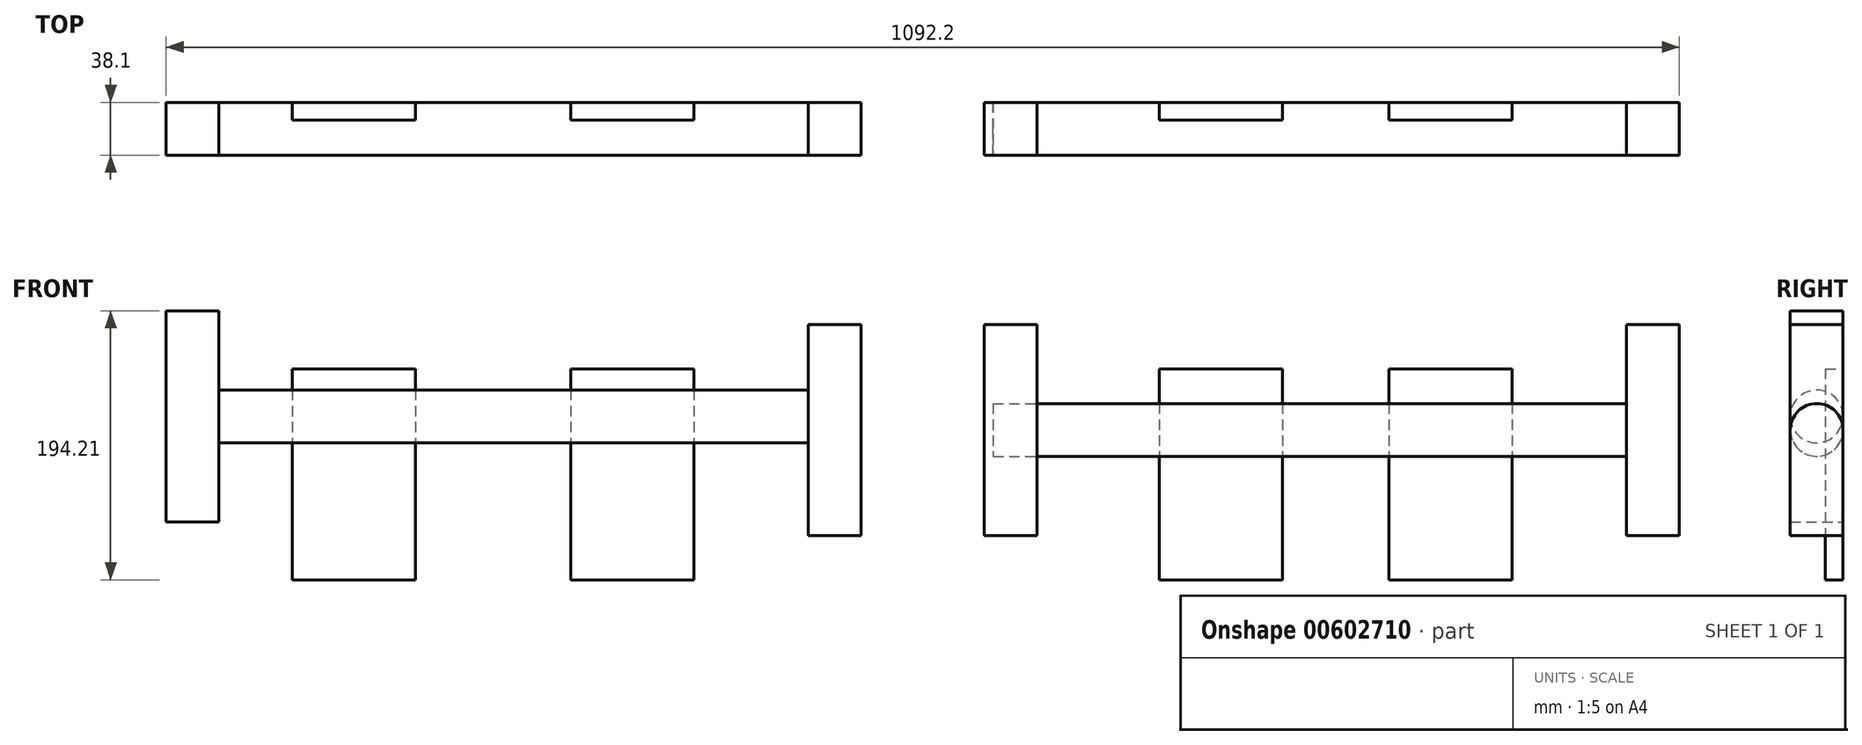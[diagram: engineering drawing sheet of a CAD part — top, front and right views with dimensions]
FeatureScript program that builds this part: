
annotation { "Feature Type Name" : "Feature", "Feature Type Description" : "" }
export const myFeature = defineFeature(function(context is Context, id is Id, definition is map)
    precondition{}
    {
        {
            var Q0;
            Q0=qCreatedBy(makeId("Front.planeOp"),FACE);
            var sketch = newSketch(context, id + "F0", { "sketchPlane" : qUnion([Q0])});
            skLineSegment(sketch, "E0.bottom", {"start": v(-201.81, 41.8) * mm, "end": v(-163.71, 41.8) * mm});
            skLineSegment(sketch, "E0.top", {"start": v(-201.81, -110.6) * mm, "end": v(-163.71, -110.6) * mm});
            skLineSegment(sketch, "E0.left", {"start": v(-201.81, 41.8) * mm, "end": v(-201.81, -110.6) * mm});
            skLineSegment(sketch, "E0.right", {"start": v(-163.71, 41.8) * mm, "end": v(-163.71, -110.6) * mm});
            skLineSegment(sketch, "E1.bottom", {"start": v(261.74, 32.02) * mm, "end": v(299.84, 32.02) * mm});
            skLineSegment(sketch, "E1.top", {"start": v(261.74, -120.38) * mm, "end": v(299.84, -120.38) * mm});
            skLineSegment(sketch, "E1.left", {"start": v(261.74, 32.02) * mm, "end": v(261.74, -120.38) * mm});
            skLineSegment(sketch, "E1.right", {"start": v(299.84, 32.02) * mm, "end": v(299.84, -120.38) * mm});
            skLineSegment(sketch, "E2.bottom", {"start": v(388.74, 32.02) * mm, "end": v(426.84, 32.02) * mm});
            skLineSegment(sketch, "E2.top", {"start": v(388.74, -120.38) * mm, "end": v(426.84, -120.38) * mm});
            skLineSegment(sketch, "E2.left", {"start": v(388.74, 32.02) * mm, "end": v(388.74, -120.38) * mm});
            skLineSegment(sketch, "E2.right", {"start": v(426.84, 32.02) * mm, "end": v(426.84, -120.38) * mm});
            skLineSegment(sketch, "E3.bottom", {"start": v(852.29, 32.02) * mm, "end": v(890.39, 32.02) * mm});
            skLineSegment(sketch, "E3.top", {"start": v(852.29, -120.38) * mm, "end": v(890.39, -120.38) * mm});
            skLineSegment(sketch, "E3.left", {"start": v(852.29, 32.02) * mm, "end": v(852.29, -120.38) * mm});
            skLineSegment(sketch, "E3.right", {"start": v(890.39, 32.02) * mm, "end": v(890.39, -120.38) * mm});
            skLineSegment(sketch, "E4", {"start": v(261.74, 32.02) * mm, "end": v(919.35, 32.02) * mm, "construction": true});
            skPoint(sketch, "E4.endSnap0", {"position": v(407.79, 32.02) * mm});
            skLineSegment(sketch, "E5", {"start": v(-201.81, 41.8) * mm, "end": v(299.84, 32.02) * mm, "construction": true});
            skSolve(sketch);
        }
        {
            var Q0;
            Q0=makeQuery(id+"F0.imprint","IMPRINT",FACE,{"disambiguationData":[TD([[makeQuery(id+"F0.imprint","IMPRINT",EDGE,{"derivedFrom":sQuery(id+"F0.wireOp",EDGE,"E0.bottom")}),-1.0]])]});
            var Q1;
            Q1=makeQuery(id+"F0.imprint","IMPRINT",FACE,{"disambiguationData":[TD([[makeQuery(id+"F0.imprint","IMPRINT",EDGE,{"derivedFrom":sQuery(id+"F0.wireOp",EDGE,"E1.bottom")}),-1.0]])]});
            var Q2;
            Q2=makeQuery(id+"F0.imprint","IMPRINT",FACE,{"disambiguationData":[TD([[makeQuery(id+"F0.imprint","IMPRINT",EDGE,{"derivedFrom":sQuery(id+"F0.wireOp",EDGE,"E2.bottom")}),-1.0]])]});
            var Q3;
            Q3=makeQuery(id+"F0.imprint","IMPRINT",FACE,{"disambiguationData":[TD([[makeQuery(id+"F0.imprint","IMPRINT",EDGE,{"derivedFrom":sQuery(id+"F0.wireOp",EDGE,"E3.bottom")}),-1.0]])]});
            extrude(context, id + "F1", {"entities" : qUnion([Q0, Q1, Q2, Q3]), "depth" : 38.1 * mm, "offsetDistance" : 25.4 * mm});
        }
        {
            var Q0;
            Q0=makeQuery(id+"F1.opExtrude","SWEPT_FACE",FACE,{"disambiguationData":[OSD([sQuery(id+"F0.wireOp",EDGE,"E0.right")])]});
            var sketch = newSketch(context, id + "F2", { "sketchPlane" : qUnion([Q0])});
            skCircle(sketch, "E6", {"center": v(-19.05, -34.4) * mm, "radius": 19.05 * mm});
            skPoint(sketch, "E6.centerSnap0", {"position": v(0, -34.4) * mm});
            skPoint(sketch, "E6.centerSnap1", {"position": v(-19.05, -110.6) * mm});
            skSolve(sketch);
        }
        {
            var Q0;
            {var subQ0=sQuery(id+"F2.wireOp",EDGE,"E6");var subQ1=sQuery(id+"F0.wireOp",EDGE,"E0.right");var subQ2=makeQuery(id+"F2.imprint","INTERSECT",VERTEX,{"derivedFrom":[makeQuery(id+"F1.opExtrude","CAP_EDGE",EDGE,{"disambiguationData":[OSD([subQ1])],"isStart":true}),subQ0]});Q0=makeQuery(id+"F2.imprint","IMPRINT",FACE,{"disambiguationData":[TD([[makeQuery(id+"F2.imprint","IMPRINT",EDGE,{"disambiguationData":[TD([[subQ2,-1.0]])],"derivedFrom":subQ0}),1.0]])]});}
            extrude(context, id + "F3", {"entities" : qUnion([Q0]), "operationType" : NewBodyOperationType.ADD, "depth" : 457.2 * mm, "offsetDistance" : 25.4 * mm});
        }
        {
            var Q0;
            Q0=makeQuery(id+"F1.opExtrude","SWEPT_FACE",FACE,{"disambiguationData":[OSD([sQuery(id+"F0.wireOp",EDGE,"E3.left")])]});
            var sketch = newSketch(context, id + "F4", { "sketchPlane" : qUnion([Q0])});
            skPoint(sketch, "E7.centerSnap0", {"position": v(38.1, -44.18) * mm});
            skCircle(sketch, "E8", {"center": v(19.05, -44.18) * mm, "radius": 19.05 * mm});
            skPoint(sketch, "E8.centerSnap0", {"position": v(19.05, -120.38) * mm});
            skPoint(sketch, "E8.centerSnap1", {"position": v(0, -44.18) * mm});
            skSolve(sketch);
        }
        {
            var Q0;
            Q0 = qSketchRegion(id + "F4", true);
            extrude(context, id + "F5", {"entities" : qUnion([Q0]), "depth" : 457.2 * mm, "offsetDistance" : 25.4 * mm});
        }
        {
            var Q0;
            Q0=qCreatedBy(makeId("Front.planeOp"),FACE);
            var sketch = newSketch(context, id + "F6", { "sketchPlane" : qUnion([Q0])});
            skLineSegment(sketch, "E9.bottom", {"start": v(90.29, 0) * mm, "end": v(179.19, 0) * mm});
            skLineSegment(sketch, "E9.top", {"start": v(90.29, -152.4) * mm, "end": v(179.19, -152.4) * mm});
            skLineSegment(sketch, "E9.left", {"start": v(90.29, 0) * mm, "end": v(90.29, -152.4) * mm});
            skLineSegment(sketch, "E9.right", {"start": v(179.19, 0) * mm, "end": v(179.19, -152.4) * mm});
            skLineSegment(sketch, "E10.bottom", {"start": v(680.84, 0) * mm, "end": v(769.74, 0) * mm});
            skLineSegment(sketch, "E10.top", {"start": v(680.84, -152.4) * mm, "end": v(769.74, -152.4) * mm});
            skLineSegment(sketch, "E10.left", {"start": v(680.84, 0) * mm, "end": v(680.84, -152.4) * mm});
            skLineSegment(sketch, "E10.right", {"start": v(769.74, 0) * mm, "end": v(769.74, -152.4) * mm});
            skLineSegment(sketch, "E11.bottom", {"start": v(603.99, 0) * mm, "end": v(515.09, 0) * mm});
            skLineSegment(sketch, "E11.top", {"start": v(603.99, -152.4) * mm, "end": v(515.09, -152.4) * mm});
            skLineSegment(sketch, "E11.left", {"start": v(603.99, 0) * mm, "end": v(603.99, -152.4) * mm});
            skLineSegment(sketch, "E11.right", {"start": v(515.09, 0) * mm, "end": v(515.09, -152.4) * mm});
            skLineSegment(sketch, "E12.bottom", {"start": v(-21.91, 0) * mm, "end": v(-110.81, 0) * mm});
            skLineSegment(sketch, "E12.top", {"start": v(-21.91, -152.4) * mm, "end": v(-110.81, -152.4) * mm});
            skLineSegment(sketch, "E12.left", {"start": v(-21.91, 0) * mm, "end": v(-21.91, -152.4) * mm});
            skLineSegment(sketch, "E12.right", {"start": v(-110.81, 0) * mm, "end": v(-110.81, -152.4) * mm});
            skSolve(sketch);
        }
        {
            var Q0;
            Q0 = qSketchRegion(id + "F6", true);
            extrude(context, id + "F7", {"entities" : qUnion([Q0]), "depth" : 12.7 * mm, "offsetDistance" : 25.4 * mm});
        }
    });
